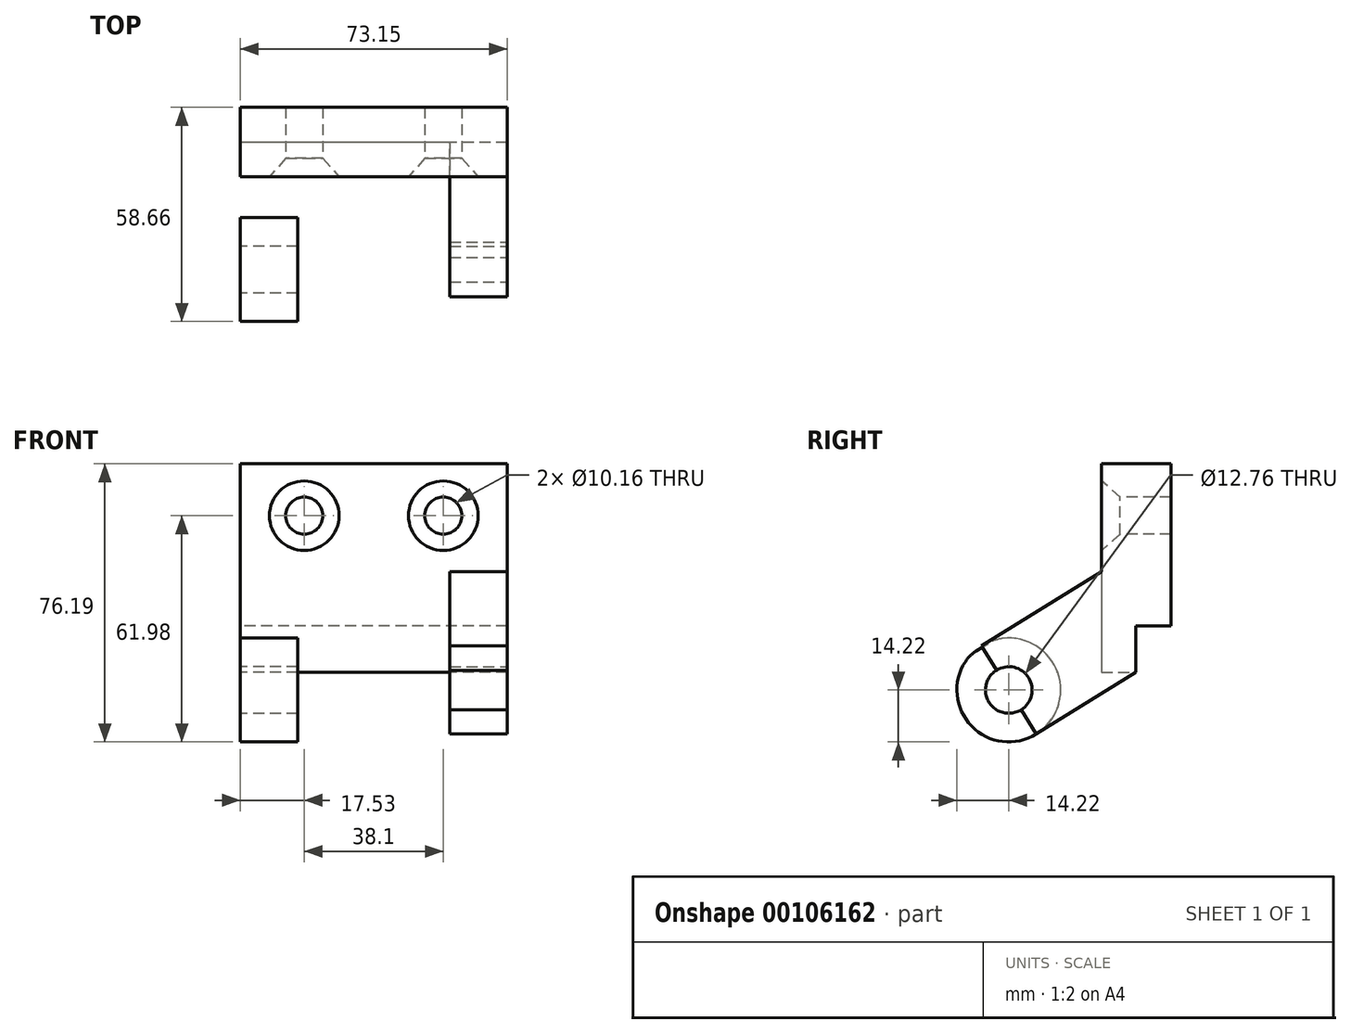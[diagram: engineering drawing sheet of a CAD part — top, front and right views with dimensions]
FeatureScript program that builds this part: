
annotation { "Feature Type Name" : "Feature", "Feature Type Description" : "" }
export const myFeature = defineFeature(function(context is Context, id is Id, definition is map)
    precondition{}
    {
        {
            var Q0;
            Q0=qCreatedBy(makeId("Right.planeOp"),FACE);
            var sketch = newSketch(context, id + "F0", { "sketchPlane" : qUnion([Q0])});
            skLineSegment(sketch, "E0.bottom", {"start": v(-4.04, 43.1) * mm, "end": v(15, 43.1) * mm});
            skLineSegment(sketch, "E0.top", {"start": v(-4.04, -14.04) * mm, "end": v(5.36, -14.04) * mm});
            skLineSegment(sketch, "E0.left", {"start": v(-4.04, 43.1) * mm, "end": v(-4.04, -14.04) * mm});
            skLineSegment(sketch, "E0.right", {"start": v(15, 43.1) * mm, "end": v(15, -14.04) * mm});
            skLineSegment(sketch, "E1.top", {"start": v(15, -14.04) * mm, "end": v(5.36, -14.04) * mm});
            skLineSegment(sketch, "E1.right", {"start": v(5.36, -14.04) * mm, "end": v(5.36, -14.04) * mm});
            skLineSegment(sketch, "E2", {"start": v(5.36, -14.04) * mm, "end": v(15, -14.04) * mm});
            skLineSegment(sketch, "E3", {"start": v(5.36, -14.04) * mm, "end": v(5.36, -1.34) * mm});
            skLineSegment(sketch, "E4", {"start": v(5.36, -1.34) * mm, "end": v(15, -1.34) * mm});
            skSolve(sketch);
        }
        {
            var Q0;
            Q0=makeQuery(id+"F0.imprint","IMPRINT",FACE,{"disambiguationData":[TD([[makeQuery(id+"F0.imprint","IMPRINT",EDGE,{"derivedFrom":sQuery(id+"F0.wireOp",EDGE,"E0.bottom")}),-1.0]])]});
            extrude(context, id + "F1", {"entities" : qUnion([Q0]), "depth" : 73.15 * mm});
        }
        {
            var Q0;
            Q0=makeQuery(id+"F1.opExtrude","SWEPT_FACE",FACE,{"disambiguationData":[OSD([sQuery(id+"F0.wireOp",EDGE,"E0.left")])]});
            var sketch = newSketch(context, id + "F2", { "sketchPlane" : qUnion([Q0])});
            skSolve(sketch);
        }
        {
            var Q0;
            {var subQ0=sQuery(id+"F0.wireOp",EDGE,"E0.left");Q0=makeQuery(id+"F2.imprint","IMPRINT",FACE,{"disambiguationData":[TD([[makeQuery(id+"F2.imprint","IMPRINT",EDGE,{"derivedFrom":makeQuery(id+"F1.opExtrude","CAP_EDGE",EDGE,{"disambiguationData":[OSD([subQ0])],"isStart":true})}),1.0]])]});}
            var sketch = newSketch(context, id + "F3", { "sketchPlane" : qUnion([Q0])});
            skLineSegment(sketch, "E5", {"start": v(0, 43.1) * mm, "end": v(17.53, 43.1) * mm});
            skLineSegment(sketch, "E6", {"start": v(17.53, 43.1) * mm, "end": v(17.53, 28.89) * mm});
            skLineSegment(sketch, "E7", {"start": v(17.53, 28.89) * mm, "end": v(0, 28.89) * mm});
            skLineSegment(sketch, "E8.bottom", {"start": v(73.15, 43.1) * mm, "end": v(55.63, 43.1) * mm});
            skLineSegment(sketch, "E8.top", {"start": v(73.15, 28.89) * mm, "end": v(55.63, 28.89) * mm});
            skLineSegment(sketch, "E8.left", {"start": v(73.15, 43.1) * mm, "end": v(73.15, 28.89) * mm});
            skLineSegment(sketch, "E8.right", {"start": v(55.63, 43.1) * mm, "end": v(55.63, 28.89) * mm});
            skCircle(sketch, "E9", {"center": v(17.53, 28.89) * mm, "radius": 5.08 * mm});
            skCircle(sketch, "E10", {"center": v(55.63, 28.89) * mm, "radius": 5.08 * mm});
            skSolve(sketch);
        }
        {
            var Q0;
            Q0=sQuery(id+"F3.wireOp",VERTEX,"E7.start");
            var Q1;
            Q1=sQuery(id+"F3.wireOp",VERTEX,"E8.top.end");
            var Q2;
            Q2=makeQuery(id+"F1.opExtrude","SWEPT_BODY",BODY,{"disambiguationData":[OSD([sQuery(id+"F0.wireOp",EDGE,"E0.bottom"),sQuery(id+"F0.wireOp",EDGE,"E0.top"),sQuery(id+"F0.wireOp",EDGE,"E0.left"),sQuery(id+"F0.wireOp",EDGE,"E0.right"),sQuery(id+"F0.wireOp",EDGE,"E1.top"),sQuery(id+"F0.wireOp",EDGE,"E1.right")])]});
            hole(context, id + "F4", {"style" : HoleStyle.C_SINK, "endStyle" : HoleEndStyle.THROUGH, "holeDiameter" : 10.16 * mm, "cSinkDiameter" : 19.05 * mm, "cSinkAngle" : 82 * degree, "locations" : qUnion([Q0, Q1]), "scope" : qUnion([Q2]), "isTappedThrough" : true});
        }
        {
            var Q0;
            Q0=makeQuery(id+"F1.opExtrude","CAP_FACE",FACE,{"disambiguationData":[OSD([sQuery(id+"F0.wireOp",EDGE,"E0.bottom"),sQuery(id+"F0.wireOp",EDGE,"E0.top"),sQuery(id+"F0.wireOp",EDGE,"E0.left"),sQuery(id+"F0.wireOp",EDGE,"E0.right"),sQuery(id+"F0.wireOp",EDGE,"E1.top"),sQuery(id+"F0.wireOp",EDGE,"E1.right")])],"isStart":false});
            var sketch = newSketch(context, id + "F5", { "sketchPlane" : qUnion([Q0])});
            skLineSegment(sketch, "E11", {"start": v(15, 43.1) * mm, "end": v(15, 27.36) * mm});
            skLineSegment(sketch, "E12.bottom", {"start": v(15, 27.36) * mm, "end": v(-29.44, 27.36) * mm});
            skLineSegment(sketch, "E12.top", {"start": v(15, -18.87) * mm, "end": v(-29.44, -18.87) * mm});
            skLineSegment(sketch, "E12.left", {"start": v(15, 27.36) * mm, "end": v(15, -18.87) * mm});
            skLineSegment(sketch, "E12.right", {"start": v(-29.44, 27.36) * mm, "end": v(-29.44, -18.87) * mm});
            skCircle(sketch, "E13", {"center": v(-29.44, -18.87) * mm, "radius": 6.38 * mm});
            skCircle(sketch, "E14", {"center": v(-29.44, -18.87) * mm, "radius": 14.22 * mm});
            skLineSegment(sketch, "E15", {"start": v(5.36, -14.04) * mm, "end": v(-21.95, -30.96) * mm});
            skLineSegment(sketch, "E16", {"start": v(-21.95, -30.96) * mm, "end": v(-36.93, -6.77) * mm});
            skPoint(sketch, "E17.endSnap0", {"position": v(-4.04, 14.53) * mm});
            skLineSegment(sketch, "E18", {"start": v(-36.93, -6.77) * mm, "end": v(-4.04, 13.6) * mm});
            skPoint(sketch, "E19.orphan", {"position": v(-4.04, 27.36) * mm});
            skSolve(sketch);
        }
        {
            var Q0;
            {var subQ0=sQuery(id+"F5.wireOp",EDGE,"E15");var subQ1=sQuery(id+"F5.wireOp",EDGE,"E12.top");var subQ2=makeQuery(id+"F5.imprint","INTERSECT",VERTEX,{"derivedFrom":[subQ1,subQ0]});Q0=makeQuery(id+"F5.imprint","IMPRINT",FACE,{"disambiguationData":[TD([[makeQuery(id+"F5.imprint","IMPRINT",EDGE,{"disambiguationData":[TD([[subQ2,-1.0]])],"derivedFrom":subQ1}),1.0]])]});}
            var Q1;
            {var subQ0=sQuery(id+"F5.wireOp",EDGE,"E18");var subQ1=sQuery(id+"F5.wireOp",EDGE,"E12.right");var subQ2=makeQuery(id+"F5.imprint","INTERSECT",VERTEX,{"derivedFrom":[subQ1,subQ0]});Q1=makeQuery(id+"F5.imprint","IMPRINT",FACE,{"disambiguationData":[TD([[makeQuery(id+"F5.imprint","IMPRINT",EDGE,{"disambiguationData":[TD([[subQ2,-1.0]])],"derivedFrom":subQ1}),-1.0]])]});}
            var Q2;
            {var subQ0=sQuery(id+"F5.wireOp",EDGE,"E16");var subQ1=sQuery(id+"F5.wireOp",EDGE,"E13");var subQ2=makeQuery(id+"F5.imprint","INTERSECT",VERTEX,{"disambiguationData":[OD(0.0)],"derivedFrom":[subQ1,subQ0]});Q2=makeQuery(id+"F5.imprint","IMPRINT",FACE,{"disambiguationData":[TD([[makeQuery(id+"F5.imprint","IMPRINT",EDGE,{"disambiguationData":[TD([[subQ2,-1.0]])],"derivedFrom":subQ1}),-1.0]])]});}
            var Q3;
            {var subQ0=sQuery(id+"F5.wireOp",EDGE,"E14");var subQ1=sQuery(id+"F5.wireOp",EDGE,"E12.top");var subQ2=makeQuery(id+"F5.imprint","INTERSECT",VERTEX,{"derivedFrom":[subQ1,subQ0]});Q3=makeQuery(id+"F5.imprint","IMPRINT",FACE,{"disambiguationData":[TD([[makeQuery(id+"F5.imprint","IMPRINT",EDGE,{"disambiguationData":[TD([[subQ2,-1.0]])],"derivedFrom":subQ1}),1.0]])]});}
            var Q4;
            {var subQ0=sQuery(id+"F5.wireOp",EDGE,"E14");var subQ1=sQuery(id+"F5.wireOp",EDGE,"E12.right");var subQ2=makeQuery(id+"F5.imprint","INTERSECT",VERTEX,{"derivedFrom":[subQ1,subQ0]});Q4=makeQuery(id+"F5.imprint","IMPRINT",FACE,{"disambiguationData":[TD([[makeQuery(id+"F5.imprint","IMPRINT",EDGE,{"disambiguationData":[TD([[subQ2,-1.0]])],"derivedFrom":subQ1}),-1.0]])]});}
            var Q5;
            {var subQ1=makeQuery(id+"F1.opExtrude","CAP_EDGE",EDGE,{"disambiguationData":[OSD([sQuery(id+"F0.wireOp",EDGE,"E0.top")])],"isStart":false});Q5=makeQuery(id+"F5.imprint","IMPRINT",FACE,{"disambiguationData":[TD([[makeQuery(id+"F5.imprint","IMPRINT",EDGE,{"derivedFrom":subQ1}),-1.0]])]});}
            var Q6;
            {var subQ0=sQuery(id+"F5.wireOp",EDGE,"E14");var subQ1=sQuery(id+"F5.wireOp",EDGE,"E12.top");var subQ2=makeQuery(id+"F5.imprint","INTERSECT",VERTEX,{"derivedFrom":[subQ1,subQ0]});Q6=makeQuery(id+"F5.imprint","IMPRINT",FACE,{"disambiguationData":[TD([[makeQuery(id+"F5.imprint","IMPRINT",EDGE,{"disambiguationData":[TD([[subQ2,-1.0]])],"derivedFrom":subQ1}),-1.0]])]});}
            extrude(context, id + "F6", {"entities" : qUnion([Q0, Q1, Q2, Q3, Q4, Q5, Q6]), "operationType" : NewBodyOperationType.ADD, "oppositeDirection" : true, "depth" : 15.75 * mm});
        }
        {
            var Q0;
            Q0=makeQuery(id+"F1.opExtrude","CAP_FACE",FACE,{"disambiguationData":[OSD([sQuery(id+"F0.wireOp",EDGE,"E0.bottom"),sQuery(id+"F0.wireOp",EDGE,"E0.top"),sQuery(id+"F0.wireOp",EDGE,"E0.left"),sQuery(id+"F0.wireOp",EDGE,"E0.right"),sQuery(id+"F0.wireOp",EDGE,"E3"),sQuery(id+"F0.wireOp",EDGE,"E4")])],"isStart":true});
            var sketch = newSketch(context, id + "F7", { "sketchPlane" : qUnion([Q0])});
            skCircle(sketch, "E20", {"center": v(29.44, -18.87) * mm, "radius": 14.22 * mm});
            skCircle(sketch, "E21", {"center": v(29.44, -18.87) * mm, "radius": 6.38 * mm});
            skLineSegment(sketch, "E22", {"start": v(19.98, -29.5) * mm, "end": v(-5.36, -14.04) * mm});
            skLineSegment(sketch, "E23", {"start": v(39.66, -8.97) * mm, "end": v(4.04, 13.02) * mm});
            skSolve(sketch);
        }
        {
            var Q0;
            Q0=makeQuery(id+"F7.imprint","IMPRINT",FACE,{"disambiguationData":[TD([[makeQuery(id+"F7.imprint","IMPRINT",EDGE,{"derivedFrom":sQuery(id+"F7.wireOp",EDGE,"E21")}),-1.0]])]});
            var Q1;
            {var subQ4=sQuery(id+"F7.wireOp",EDGE,"E22");Q1=makeQuery(id+"F7.imprint","IMPRINT",FACE,{"disambiguationData":[TD([[makeQuery(id+"F7.imprint","IMPRINT",EDGE,{"derivedFrom":subQ4}),-1.0]])]});}
            extrude(context, id + "F8", {"entities" : qUnion([Q0, Q1]), "operationType" : NewBodyOperationType.ADD, "oppositeDirection" : true, "depth" : 15.75 * mm});
        }
        {
            var Q0;
            Q0=makeQuery(id+"F6.opExtrude","SWEPT_EDGE",EDGE,{"disambiguationData":[OSD([sQuery(id+"F0.wireOp",EDGE,"E0.left"),sQuery(id+"F5.wireOp",EDGE,"E18")])]});
            var Q1;
            Q1=makeQuery(id+"F8.opExtrude","SWEPT_EDGE",EDGE,{"disambiguationData":[OSD([sQuery(id+"F0.wireOp",EDGE,"E0.left"),sQuery(id+"F7.wireOp",EDGE,"E23")])]});
            fillet(context, id + "F9", {"entities" : qUnion([Q0, Q1]), "radius" : 9.65 * mm, "tangentPropagation" : true, "allowEdgeOverflow" : false});
        }
    });
